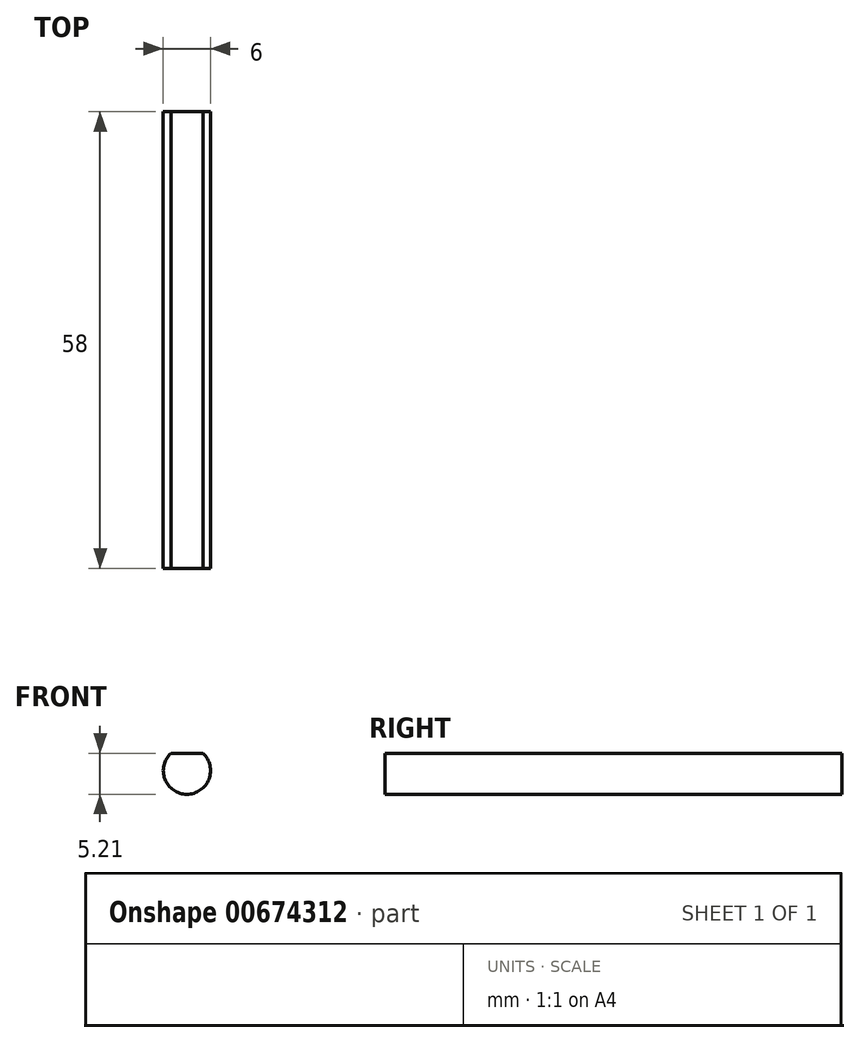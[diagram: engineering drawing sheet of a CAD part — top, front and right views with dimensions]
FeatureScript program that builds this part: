
annotation { "Feature Type Name" : "Feature", "Feature Type Description" : "" }
export const myFeature = defineFeature(function(context is Context, id is Id, definition is map)
    precondition{}
    {
        {
            var Q0;
            Q0=qCreatedBy(makeId("Front.planeOp"),FACE);
            var sketch = newSketch(context, id + "F0", { "sketchPlane" : qUnion([Q0])});
            skCircle(sketch, "E0", {"center": v(0, 0) * mm, "radius": 3 * mm});
            skSolve(sketch);
        }
        {
            var Q0;
            Q0=qSketchRegion(id+"F0",true);
            extrude(context, id + "F1", {"entities" : qUnion([Q0]), "depth" : 58 * mm, "offsetDistance" : 25 * mm});
        }
        {
            var Q0;
            Q0=makeQuery(id+"F1.opExtrude","CAP_FACE",FACE,{"disambiguationData":[OSD([sQuery(id+"F0.wireOp",EDGE,"E0")])],"isStart":false});
            var sketch = newSketch(context, id + "F2", { "sketchPlane" : qUnion([Q0])});
            skLineSegment(sketch, "E1.bottom", {"start": v(-2.03, 3.43) * mm, "end": v(2.03, 3.43) * mm});
            skLineSegment(sketch, "E1.top", {"start": v(-2.03, 2.2) * mm, "end": v(2.03, 2.2) * mm});
            skLineSegment(sketch, "E1.left", {"start": v(-2.03, 3.43) * mm, "end": v(-2.03, 2.2) * mm});
            skLineSegment(sketch, "E1.right", {"start": v(2.03, 3.43) * mm, "end": v(2.03, 2.2) * mm});
            skSolve(sketch);
        }
        {
            var Q0;
            Q0=qSketchRegion(id+"F2",true);
            extrude(context, id + "F3", {"entities" : qUnion([Q0]), "operationType" : NewBodyOperationType.REMOVE, "endBound" : BoundingType.THROUGH_ALL, "oppositeDirection" : true, "depth" : 25 * mm, "offsetDistance" : 25 * mm});
        }
    });
